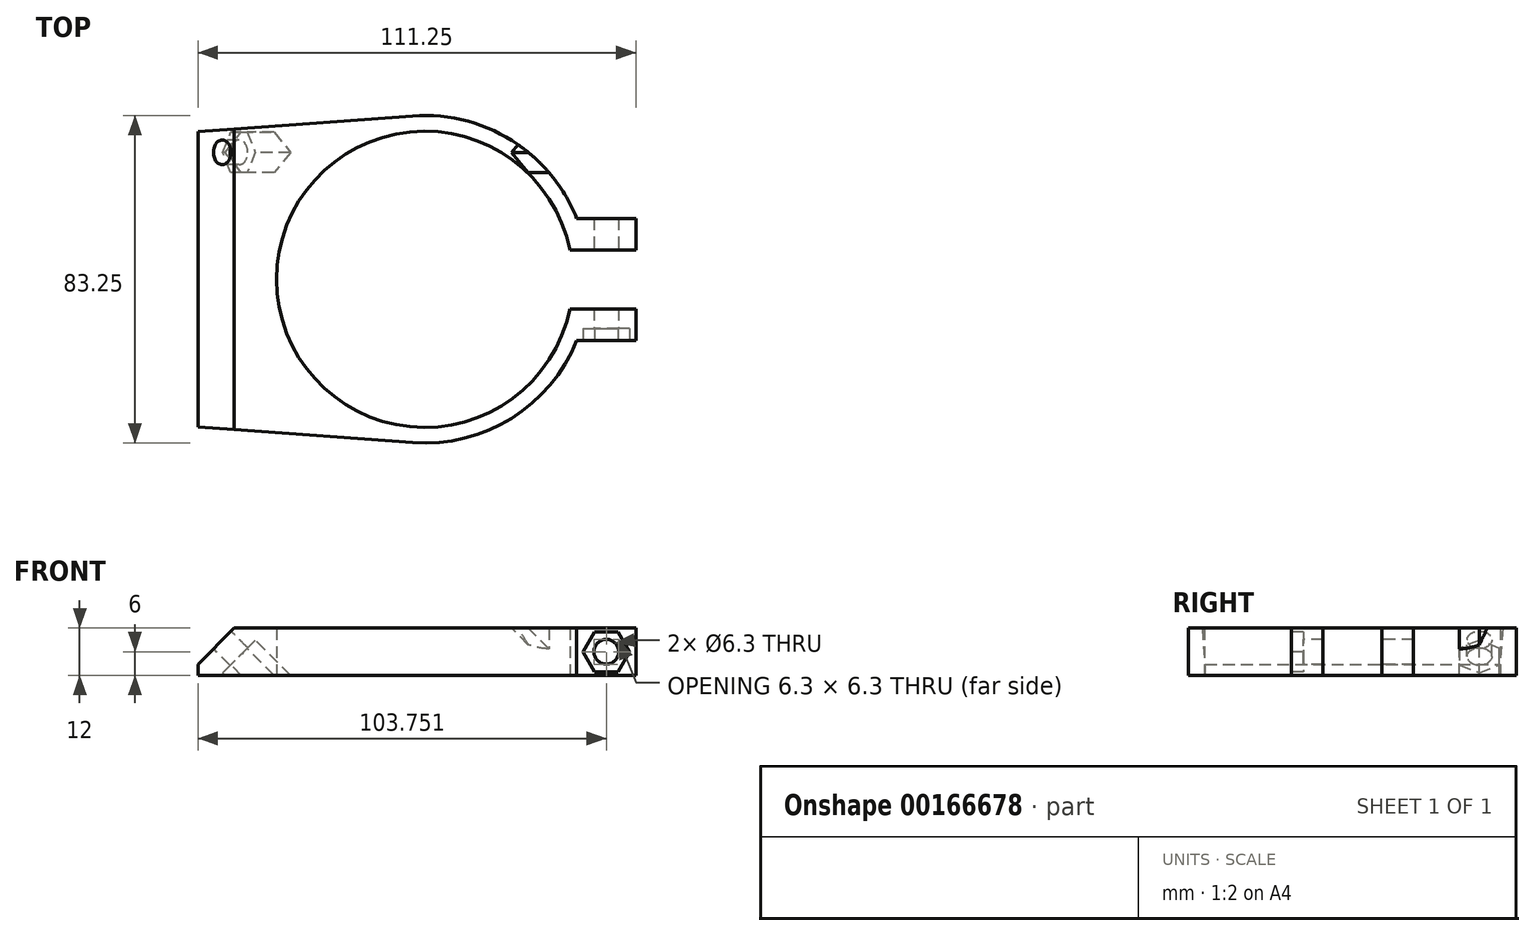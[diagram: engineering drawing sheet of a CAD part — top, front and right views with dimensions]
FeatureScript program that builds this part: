
annotation { "Feature Type Name" : "Feature", "Feature Type Description" : "" }
export const myFeature = defineFeature(function(context is Context, id is Id, definition is map)
    precondition{}
    {
        {
            var Q0;
            Q0=qCreatedBy(makeId("Top.planeOp"),FACE);
            var sketch = newSketch(context, id + "F0", { "sketchPlane" : qUnion([Q0])});
            skArc(sketch, "E0", {"start": v(36.87, 7.5) * mm, "mid": v(-37.63, 0) * mm, "end": v(36.87, -7.5) * mm});
            skArc(sketch, "E1", {"start": v(38.63, 15.5) * mm, "mid": v(-41.63, 0) * mm, "end": v(38.63, -15.5) * mm});
            skLineSegment(sketch, "E2", {"start": v(38.63, 15.5) * mm, "end": v(53.63, 15.5) * mm});
            skLineSegment(sketch, "E3", {"start": v(53.63, 15.5) * mm, "end": v(53.63, 7.5) * mm});
            skLineSegment(sketch, "E4", {"start": v(53.63, 7.5) * mm, "end": v(36.87, 7.5) * mm});
            skLineSegment(sketch, "E5", {"start": v(36.87, -7.5) * mm, "end": v(53.63, -7.5) * mm});
            skLineSegment(sketch, "E6", {"start": v(53.63, -7.5) * mm, "end": v(53.63, -15.5) * mm});
            skLineSegment(sketch, "E7", {"start": v(53.63, -15.5) * mm, "end": v(38.63, -15.5) * mm});
            skLineSegment(sketch, "E8", {"start": v(-57.63, 37.5) * mm, "end": v(-57.62, -37.5) * mm});
            skLineSegment(sketch, "E9", {"start": v(-57.63, 37.5) * mm, "end": v(-3.05, 41.51) * mm});
            skLineSegment(sketch, "E10", {"start": v(-57.63, -37.5) * mm, "end": v(-3.05, -41.51) * mm});
            skArc(sketch, "E11", {"start": v(-3.05, 41.51) * mm, "mid": v(-41.63, 0) * mm, "end": v(-3.05, -41.51) * mm});
            skSolve(sketch);
        }
        {
            var Q0;
            Q0 = qSketchRegion(id + "F0", true);
            extrude(context, id + "F1", {"entities" : qUnion([Q0]), "depth" : 12 * mm});
        }
        {
            var Q0;
            Q0=qCreatedBy(makeId("Front.planeOp"),FACE);
            var sketch = newSketch(context, id + "F2", { "sketchPlane" : qUnion([Q0])});
            skLineSegment(sketch, "E12", {"start": v(-66.5, -6.03) * mm, "end": v(-39.63, 20.84) * mm, "construction": true});
            skLineSegment(sketch, "E13", {"start": v(-53.06, 7.4) * mm, "end": v(-93.18, 47.52) * mm, "construction": true});
            skLineSegment(sketch, "E14", {"start": v(-57.66, 2.8) * mm, "end": v(-48.46, 12) * mm});
            skLineSegment(sketch, "E15", {"start": v(-48.46, 12) * mm, "end": v(-48.46, 26.05) * mm});
            skLineSegment(sketch, "E16", {"start": v(-48.46, 26.05) * mm, "end": v(-57.66, 26.05) * mm});
            skLineSegment(sketch, "E17", {"start": v(-57.66, 26.05) * mm, "end": v(-57.66, 2.8) * mm});
            skLineSegment(sketch, "E18", {"start": v(0, 0) * mm, "end": v(-112.7, 0) * mm, "construction": true});
            skSolve(sketch);
        }
        {
            var Q0;
            Q0 = qSketchRegion(id + "F2", true);
            extrude(context, id + "F3", {"entities" : qUnion([Q0]), "operationType" : NewBodyOperationType.REMOVE, "oppositeDirection" : true, "depth" : 100 * mm, "symmetric" : true});
        }
        {
            var Q0;
            Q0=makeQuery(id+"F3.boolean.opBoolean","COPY",FACE,{"derivedFrom":makeQuery(id+"F3.opExtrude","SWEPT_FACE",FACE,{"disambiguationData":[OSD([sQuery(id+"F2.wireOp",EDGE,"E14")])]})});
            var sketch = newSketch(context, id + "F4", { "sketchPlane" : qUnion([Q0])});
            skCircle(sketch, "E19", {"center": v(-32.26, 30) * mm, "radius": 3.15 * mm});
            skCircle(sketch, "E20", {"center": v(-32.26, -30) * mm, "radius": 3.15 * mm});
            skLineSegment(sketch, "E21", {"start": v(-32.26, 30) * mm, "end": v(-32.26, -30) * mm, "construction": true});
            skSolve(sketch);
        }
        {
            var Q0;
            Q0 = qSketchRegion(id + "F4", true);
            extrude(context, id + "F5", {"entities" : qUnion([Q0]), "operationType" : NewBodyOperationType.REMOVE, "endBound" : BoundingType.THROUGH_ALL, "oppositeDirection" : true, "depth" : 25 * mm});
        }
        {
            var Q0;
            Q0=makeQuery(id+"F3.boolean.opBoolean","COPY",FACE,{"derivedFrom":makeQuery(id+"F3.opExtrude","SWEPT_FACE",FACE,{"disambiguationData":[OSD([sQuery(id+"F2.wireOp",EDGE,"E14")])]})});
            cPlane(context, id + "F6", {"entities" : qUnion([Q0]), "cplaneType" : CPlaneType.OFFSET, "offset" : 6 * mm, "oppositeDirection" : true, "width" : 150 * mm, "height" : 150 * mm});
        }
        {
            var Q0;
            Q0=qCreatedBy(id+"F6.planeOp",FACE);
            var sketch = newSketch(context, id + "F7", { "sketchPlane" : qUnion([Q0])});
            skCircle(sketch, "E22.cCircle", {"center": v(-32.26, 30) * mm, "radius": 5.1 * mm, "construction": true});
            skLineSegment(sketch, "E22.0", {"start": v(-27.16, 27.06) * mm, "end": v(-32.26, 24.11) * mm});
            skLineSegment(sketch, "E22.1", {"start": v(-32.26, 24.11) * mm, "end": v(-37.36, 27.06) * mm});
            skLineSegment(sketch, "E22.2", {"start": v(-37.36, 27.06) * mm, "end": v(-37.36, 32.94) * mm});
            skLineSegment(sketch, "E22.3", {"start": v(-37.36, 32.94) * mm, "end": v(-32.26, 35.89) * mm});
            skLineSegment(sketch, "E22.4", {"start": v(-32.26, 35.89) * mm, "end": v(-27.16, 32.94) * mm});
            skLineSegment(sketch, "E22.5", {"start": v(-27.16, 32.94) * mm, "end": v(-27.16, 27.06) * mm});
            skPoint(sketch, "E22.0.midPoint", {"position": v(-29.71, 25.58) * mm});
            skCircle(sketch, "E23.cCircle", {"center": v(-32.26, -30) * mm, "radius": 5.1 * mm, "construction": true});
            skLineSegment(sketch, "E23.0", {"start": v(-27.16, -32.94) * mm, "end": v(-32.26, -35.89) * mm});
            skLineSegment(sketch, "E23.1", {"start": v(-32.26, -35.89) * mm, "end": v(-37.36, -32.94) * mm});
            skLineSegment(sketch, "E23.2", {"start": v(-37.36, -32.94) * mm, "end": v(-37.36, -27.06) * mm});
            skLineSegment(sketch, "E23.3", {"start": v(-37.36, -27.06) * mm, "end": v(-32.26, -24.11) * mm});
            skLineSegment(sketch, "E23.4", {"start": v(-32.26, -24.11) * mm, "end": v(-27.16, -27.06) * mm});
            skLineSegment(sketch, "E23.5", {"start": v(-27.16, -27.06) * mm, "end": v(-27.16, -32.94) * mm});
            skPoint(sketch, "E23.0.midPoint", {"position": v(-29.71, -34.42) * mm});
            skSolve(sketch);
        }
        {
            var Q0;
            Q0 = qSketchRegion(id + "F7", true);
            extrude(context, id + "F8", {"entities" : qUnion([Q0]), "operationType" : NewBodyOperationType.REMOVE, "endBound" : BoundingType.THROUGH_ALL, "oppositeDirection" : true, "depth" : 25 * mm});
        }
        {
            var Q0;
            Q0=makeQuery(id+"F1.opExtrude","SWEPT_FACE",FACE,{"disambiguationData":[OSD([sQuery(id+"F0.wireOp",EDGE,"E7")])]});
            var sketch = newSketch(context, id + "F9", { "sketchPlane" : qUnion([Q0])});
            skLineSegment(sketch, "E24", {"start": v(46.13, 17.35) * mm, "end": v(46.13, -5.35) * mm, "construction": true});
            skLineSegment(sketch, "E25", {"start": v(75.17, 6) * mm, "end": v(107.25, 6) * mm, "construction": true});
            skCircle(sketch, "E26", {"center": v(46.13, 6) * mm, "radius": 3.15 * mm});
            skSolve(sketch);
        }
        {
            var Q0;
            Q0 = qSketchRegion(id + "F9", true);
            extrude(context, id + "F10", {"entities" : qUnion([Q0]), "operationType" : NewBodyOperationType.REMOVE, "endBound" : BoundingType.THROUGH_ALL, "oppositeDirection" : true, "depth" : 25 * mm});
        }
        {
            var Q0;
            Q0=makeQuery(id+"F1.opExtrude","SWEPT_FACE",FACE,{"disambiguationData":[OSD([sQuery(id+"F0.wireOp",EDGE,"E7")])]});
            var sketch = newSketch(context, id + "F11", { "sketchPlane" : qUnion([Q0])});
            skCircle(sketch, "E27.cCircle", {"center": v(46.13, 6) * mm, "radius": 5.1 * mm, "construction": true});
            skLineSegment(sketch, "E27.0", {"start": v(52.02, 6) * mm, "end": v(49.08, 0.9) * mm});
            skLineSegment(sketch, "E27.1", {"start": v(49.08, 0.9) * mm, "end": v(43.19, 0.9) * mm});
            skLineSegment(sketch, "E27.2", {"start": v(43.19, 0.9) * mm, "end": v(40.24, 6) * mm});
            skLineSegment(sketch, "E27.3", {"start": v(40.24, 6) * mm, "end": v(43.19, 11.1) * mm});
            skLineSegment(sketch, "E27.4", {"start": v(43.19, 11.1) * mm, "end": v(49.08, 11.1) * mm});
            skLineSegment(sketch, "E27.5", {"start": v(49.08, 11.1) * mm, "end": v(52.02, 6) * mm});
            skPoint(sketch, "E27.0.midPoint", {"position": v(50.55, 3.45) * mm});
            skSolve(sketch);
        }
        {
            var Q0;
            Q0 = qSketchRegion(id + "F11", true);
            extrude(context, id + "F12", {"entities" : qUnion([Q0]), "operationType" : NewBodyOperationType.REMOVE, "oppositeDirection" : true, "depth" : 3 * mm});
        }
    });
